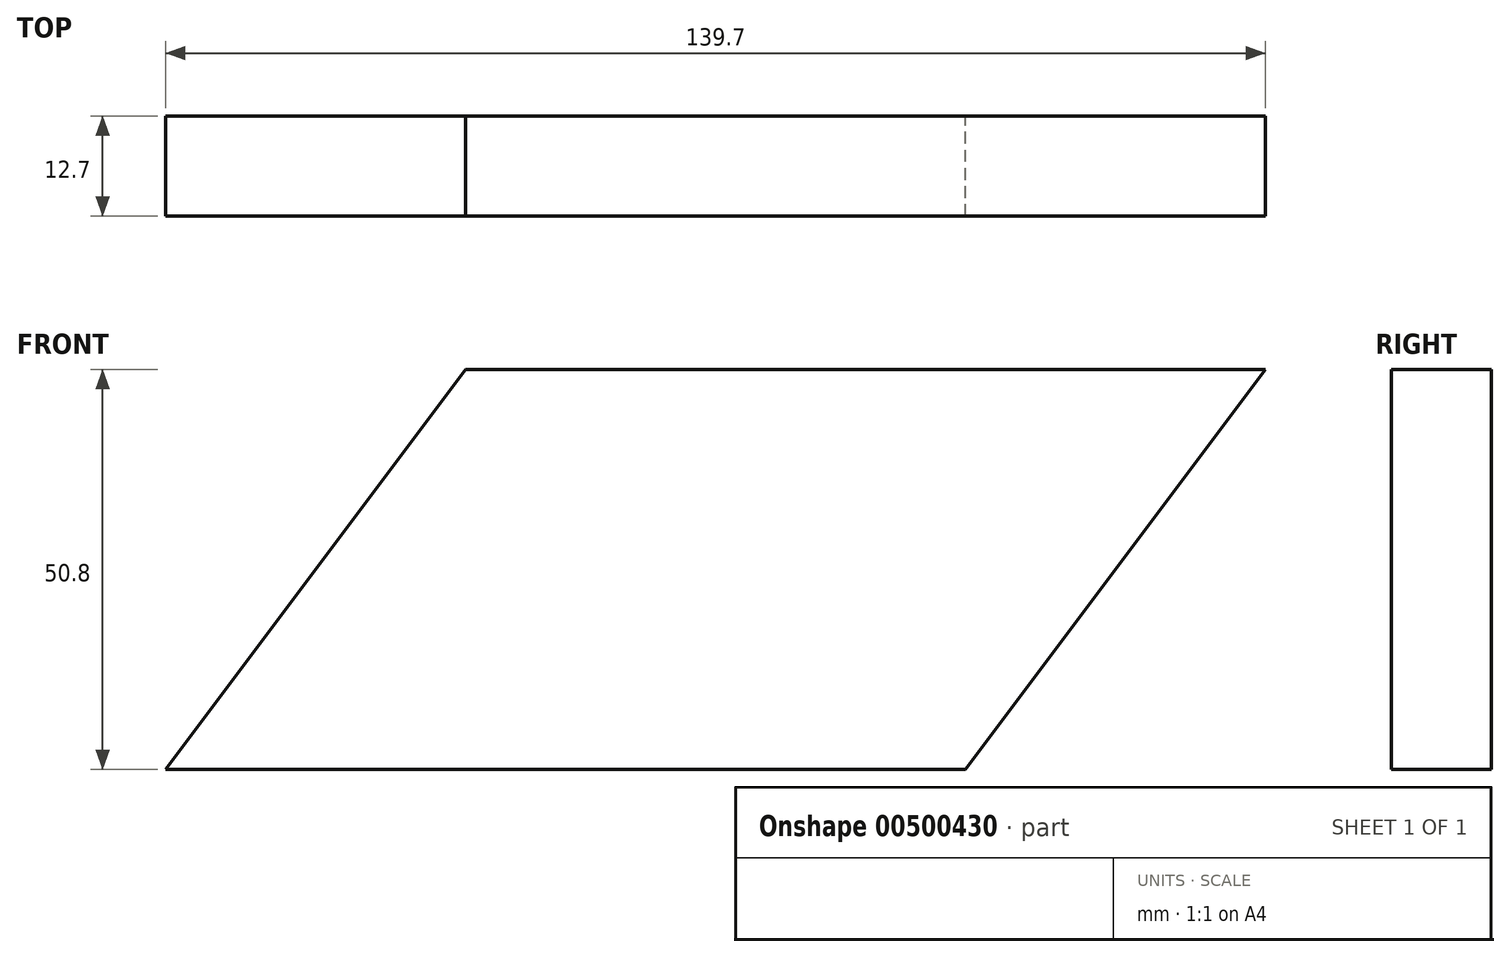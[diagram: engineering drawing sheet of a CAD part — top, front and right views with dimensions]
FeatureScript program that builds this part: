
annotation { "Feature Type Name" : "Feature", "Feature Type Description" : "" }
export const myFeature = defineFeature(function(context is Context, id is Id, definition is map)
    precondition{}
    {
        {
            var Q0;
            Q0=qCreatedBy(makeId("Front.planeOp"),FACE);
            var sketch = newSketch(context, id + "F0", { "sketchPlane" : qUnion([Q0])});
            skLineSegment(sketch, "E0.bottom", {"start": v(-31.75, 25.4) * mm, "end": v(31.75, 25.4) * mm});
            skLineSegment(sketch, "E0.top", {"start": v(-31.75, -25.4) * mm, "end": v(31.75, -25.4) * mm});
            skLineSegment(sketch, "E0.left", {"start": v(-31.75, 25.4) * mm, "end": v(-31.75, -25.4) * mm});
            skLineSegment(sketch, "E0.right", {"start": v(31.75, 25.4) * mm, "end": v(31.75, -25.4) * mm});
            skPoint(sketch, "E0.middle", {"position": v(0, 0) * mm});
            skLineSegment(sketch, "E1", {"start": v(31.75, 25.4) * mm, "end": v(69.85, 25.4) * mm});
            skLineSegment(sketch, "E2", {"start": v(69.85, 25.4) * mm, "end": v(31.75, -25.4) * mm});
            skLineSegment(sketch, "E3", {"start": v(-31.75, -25.4) * mm, "end": v(-69.85, -25.4) * mm});
            skLineSegment(sketch, "E4", {"start": v(-69.85, -25.4) * mm, "end": v(-31.75, 25.4) * mm});
            skSolve(sketch);
        }
        {
            var Q0;
            Q0=makeQuery(id+"F0.imprint","IMPRINT",FACE,{"disambiguationData":[TD([[makeQuery(id+"F0.imprint","IMPRINT",EDGE,{"derivedFrom":sQuery(id+"F0.wireOp",EDGE,"E0.left")}),-1.0]])]});
            var Q1;
            Q1=makeQuery(id+"F0.imprint","IMPRINT",FACE,{"disambiguationData":[TD([[makeQuery(id+"F0.imprint","IMPRINT",EDGE,{"derivedFrom":sQuery(id+"F0.wireOp",EDGE,"E0.bottom")}),-1.0]])]});
            var Q2;
            Q2=makeQuery(id+"F0.imprint","IMPRINT",FACE,{"disambiguationData":[TD([[makeQuery(id+"F0.imprint","IMPRINT",EDGE,{"derivedFrom":sQuery(id+"F0.wireOp",EDGE,"E0.right")}),1.0]])]});
            extrude(context, id + "F1", {"entities" : qUnion([Q0, Q1, Q2]), "endBound" : BoundingType.SYMMETRIC, "depth" : 12.7 * mm});
        }
    });
